# Revit family: M_Plug Valve - 15-50 mm
name_source: partatom
category: Pipe Accessories
revit_build: Autodesk Revit MEP 2014 (Build: 20130308_1515(x64)
units: mm (PartAtom-declared; Revit-internal decimal feet)

## types (6) — shared parameters
Valve Material = PVC, Green

## per-type parameters (varying)
- 15 mm: Adapter Width=29 mm  [stored 0.0951444 ft]; Diameter 1=43 mm  [stored 0.141076 ft]; Diameter 2=45 mm  [stored 0.147638 ft]; Diameter 3=10 mm  [stored 0.0328084 ft]; Diameter 4=5 mm  [stored 0.0164042 ft]; H2=55 mm; H3=25 mm  [stored 0.082021 ft]; Half Adapter Width=15 mm  [stored 0.0492126 ft]; Half Lever Length=81 mm; Half Valve Length=42 mm; Height 1=33 mm  [stored 0.108268 ft]; Height 2=29 mm  [stored 0.0951444 ft]; Height 3=38 mm  [stored 0.124672 ft]; Height 4=64 mm; K Coefficient=0.33; Lever Diameter=8 mm  [stored 0.0262467 ft]; Lever Length=162 mm; Lever Radius=4 mm  [stored 0.0131234 ft]; Nominal Radius=8 mm; Open Height=68 mm; Outside Diameter=43 mm  [stored 0.141076 ft]; Outside Radius=22 mm; Radius 2=23 mm; Radius 3=5 mm  [stored 0.0164042 ft]; Radius 4=3 mm  [stored 0.00984252 ft]; Valve Length=83 mm
- 20 mm: Adapter Width=29 mm  [stored 0.0951444 ft]; Diameter 1=43 mm  [stored 0.141076 ft]; Diameter 2=45 mm  [stored 0.147638 ft]; Diameter 3=10 mm  [stored 0.0328084 ft]; Diameter 4=5 mm  [stored 0.0164042 ft]; H2=55 mm; H3=25 mm  [stored 0.082021 ft]; Half Adapter Width=15 mm  [stored 0.0492126 ft]; Half Lever Length=81 mm; Half Valve Length=42 mm; Height 1=33 mm  [stored 0.108268 ft]; Height 2=29 mm  [stored 0.0951444 ft]; Height 3=38 mm  [stored 0.124672 ft]; Height 4=64 mm; K Coefficient=1.67; Lever Diameter=8 mm  [stored 0.0262467 ft]; Lever Length=162 mm; Lever Radius=4 mm  [stored 0.0131234 ft]; Nominal Radius=10 mm; Open Height=68 mm; Outside Diameter=43 mm  [stored 0.141076 ft]; Outside Radius=22 mm; Radius 2=23 mm; Radius 3=5 mm  [stored 0.0164042 ft]; Radius 4=3 mm  [stored 0.00984252 ft]; Valve Length=83 mm
- 25 mm: Adapter Width=41 mm  [stored 0.134514 ft]; Diameter 1=56 mm; Diameter 2=64 mm; Diameter 3=14 mm  [stored 0.0459318 ft]; Diameter 4=7 mm  [stored 0.0229659 ft]; H2=79 mm; H3=35 mm; Half Adapter Width=21 mm; Half Lever Length=111 mm; Half Valve Length=59 mm; Height 1=44 mm  [stored 0.144357 ft]; Height 2=37 mm  [stored 0.121391 ft]; Height 3=48 mm  [stored 0.15748 ft]; Height 4=82 mm; K Coefficient=0.69; Lever Diameter=10 mm  [stored 0.0328084 ft]; Lever Length=222 mm; Lever Radius=5 mm  [stored 0.0164042 ft]; Nominal Radius=13 mm; Open Height=87 mm; Outside Diameter=56 mm; Outside Radius=28 mm  [stored 0.0918635 ft]; Radius 2=32 mm  [stored 0.104987 ft]; Radius 3=7 mm  [stored 0.0229659 ft]; Radius 4=4 mm  [stored 0.0131234 ft]; Valve Length=118 mm
- 40 mm: Adapter Width=49 mm  [stored 0.160761 ft]; Diameter 1=60 mm; Diameter 2=75 mm; Diameter 3=17 mm; Diameter 4=9 mm  [stored 0.0295276 ft]; H2=93 mm; H3=42 mm; Half Adapter Width=25 mm  [stored 0.082021 ft]; Half Lever Length=159 mm; Half Valve Length=70 mm; Height 1=41 mm  [stored 0.134514 ft]; Height 2=39 mm  [stored 0.127953 ft]; Height 3=51 mm; Height 4=87 mm; K Coefficient=0.29; Lever Diameter=10 mm  [stored 0.0328084 ft]; Lever Length=318 mm; Lever Radius=5 mm  [stored 0.0164042 ft]; Nominal Radius=20 mm; Open Height=93 mm; Outside Diameter=60 mm; Outside Radius=30 mm  [stored 0.0984252 ft]; Radius 2=38 mm  [stored 0.124672 ft]; Radius 3=9 mm  [stored 0.0295276 ft]; Radius 4=5 mm  [stored 0.0164042 ft]; Valve Length=140 mm
- 50 mm: Adapter Width=58 mm; Diameter 1=77 mm; Diameter 2=89 mm; Diameter 3=20 mm  [stored 0.0656168 ft]; Diameter 4=10 mm  [stored 0.0328084 ft]; H2=110 mm; H3=50 mm  [stored 0.164042 ft]; Half Adapter Width=29 mm  [stored 0.0951444 ft]; Half Lever Length=229 mm; Half Valve Length=83 mm; Height 1=52 mm; Height 2=48 mm  [stored 0.15748 ft]; Height 3=64 mm; Height 4=110 mm; K Coefficient=0.27; Lever Diameter=11 mm  [stored 0.0360892 ft]; Lever Length=457 mm; Lever Radius=6 mm; Nominal Radius=25 mm; Open Height=118 mm; Outside Diameter=77 mm; Outside Radius=39 mm  [stored 0.127953 ft]; Radius 2=45 mm  [stored 0.147638 ft]; Radius 3=10 mm  [stored 0.0328084 ft]; Radius 4=5 mm  [stored 0.0164042 ft]; Valve Length=165 mm
- 32 mm: Adapter Width=49 mm  [stored 0.160761 ft]; Diameter 1=60 mm; Diameter 2=75 mm; Diameter 3=17 mm; Diameter 4=9 mm  [stored 0.0295276 ft]; H2=93 mm; H3=42 mm; Half Adapter Width=25 mm  [stored 0.082021 ft]; Half Lever Length=159 mm; Half Valve Length=70 mm; Height 1=41 mm  [stored 0.134514 ft]; Height 2=39 mm  [stored 0.127953 ft]; Height 3=51 mm; Height 4=87 mm; K Coefficient=0.29; Lever Diameter=10 mm  [stored 0.0328084 ft]; Lever Length=318 mm; Lever Radius=5 mm  [stored 0.0164042 ft]; Nominal Radius=16 mm; Open Height=93 mm; Outside Diameter=60 mm; Outside Radius=30 mm  [stored 0.0984252 ft]; Radius 2=38 mm  [stored 0.124672 ft]; Radius 3=9 mm  [stored 0.0295276 ft]; Radius 4=5 mm  [stored 0.0164042 ft]; Valve Length=140 mm

note: column(s) folded — value = type name in every type: Nominal Diameter

note: [stored X ft] marks values corroborated as IEEE doubles in the binary element streams (Revit-internal decimal feet)

## geometry (parser evidence)
native form markers: Blend x2, Sweep x3
no freeform markers — native parametric forms only
